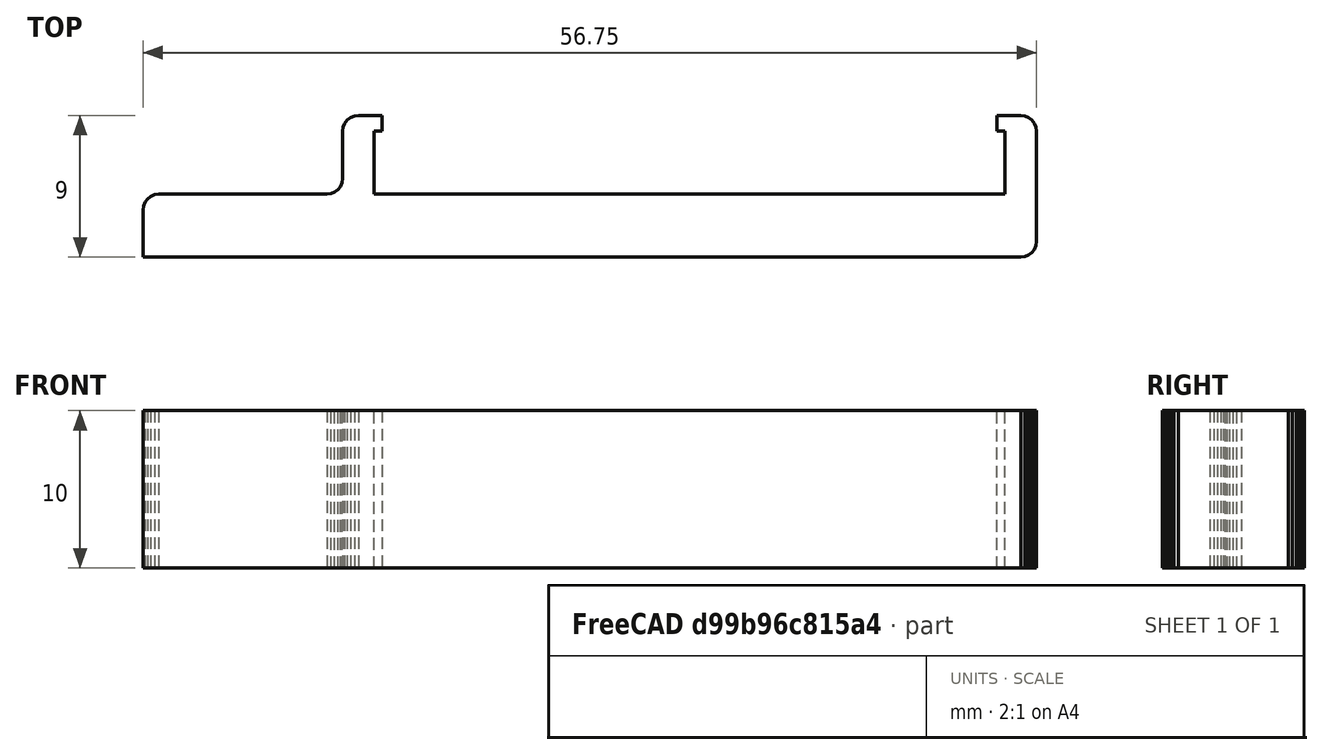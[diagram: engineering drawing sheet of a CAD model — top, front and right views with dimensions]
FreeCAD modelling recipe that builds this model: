
FCSTD DOCUMENT  (FreeCAD 0.22R35989 (Git))
Label: ender 3 v3 se rpi mount
License: All rights reserved
LicenseURL: http://en.wikipedia.org/wiki/All_rights_reserved
objects: Part::Feature×2, Mesh::Feature×1, Part::Refine×1, PartDesign::FeatureBase×1, Sketcher::SketchObject×1, PartDesign::Pocket×1, PartDesign::Body×1
note: 8 computed .brp shape members not serialized (recipe doc carries the construction recipe); baked Part::Feature solids carry a one-line shape summary decoded from their .brp

FEATURE [Mesh::Feature] CableHolder
FEATURE [Part::Feature] CableHolder001
  shape: bbox 56.75 x 35.5 x 10 mm, 328 faces, 0 solids (baked)
FEATURE [Part::Refine] CableHolder002
  Source = -> CableHolder001
FEATURE [Part::Feature] CableHolder002_solid  label="CableHolder002 (Solid)"
  shape: bbox 56.75 x 35.5 x 10 mm, 84 faces (baked)
FEATURE [PartDesign::FeatureBase] BaseFeature
  BaseFeature = -> CableHolder002_solid
  Suppressed = false
FEATURE [Sketcher::SketchObject] Sketch
  ExternalGeometry = -> [BaseFeature]
  FullyConstrained = false
  MapMode = 5
  Placement = pos=(0,0,10) rot=(0,0,1;0rad)
  Support = -> [BaseFeature]
  sketch-geometry (4):
    g0: LineSegment StartX=-17.6833 StartY=0.0686816 StartZ=0 EndX=-17.6833 EndY=-26.922 EndZ=0
    g1: LineSegment StartX=-17.6833 StartY=-26.922 StartZ=0 EndX=0.316689 EndY=-26.922 EndZ=0
    g2: LineSegment StartX=0.316689 StartY=-26.922 StartZ=0 EndX=0.316689 EndY=0.0686816 EndZ=0
    g3: LineSegment StartX=0.316689 StartY=0.0686816 StartZ=0 EndX=-17.6833 EndY=0.0686816 EndZ=0
  constraints (10):
    c: Coincident(g0,g1)
    c: Coincident(g1,g2)
    c: Coincident(g2,g3)
    c: Coincident(g3,g0)
    c: Vertical(g0)
    c: Vertical(g2)
    c: Horizontal(g1)
    c: Horizontal(g3)
    c: Coincident(g2,g-3)
    c: DistanceX(g0,g-4) = 0
FEATURE [PartDesign::Pocket] Pocket
  BaseFeature = -> BaseFeature
  Direction = (0,0,-1)
  Length = 5
  Length2 = 5
  Profile = -> Sketch
  ReferenceAxis = -> Sketch [N_Axis]
  Suppressed = false
  Type = 1
FEATURE [PartDesign::Body] Body
  BaseFeature = -> CableHolder002_solid
  Group = -> [BaseFeature,Sketch,Pocket]
  Origin = -> Origin
  Tip = -> Pocket
